# Revit family: Urinal-Monoblock-BackWaterInlet-Vitra_PluralSeries_7809B003-5330
name_source: partatom
category: Plumbing Fixtures
revit_build: Autodesk Revit 2017 (Build: 20160225_1515(x64)
units: mm (PartAtom-declared; Revit-internal decimal feet)

## family parameters
Cut with Voids When Loaded = No
Host = Face
OmniClass Number = 23.45.05.21.11.21
OmniClass Title = Urinals
Part Type = Normal
Room Calculation Point = No
Round Connector Dimension = Use Diameter
Shared = Yes

## types (10) — shared parameters
BIMobject category = Urinals
CW Connection = Yes
Default Elevation = 650 mm  [stored 2.13255 ft]
Description = VitrA Plural Monoblock urinal with integrated flushing mechanism Back inlet,
Design country = Turkey
HW Connection = No
IFC Classification = Sanitary Terminal
Main Material = Ceramic
Manufacturer = Vitra
Manufacturer name = Vitra
Masterformat 2014 Code = 22 41 13.16
Masterformat 2014 Description = Residential Urinals
MountingType = Face Mounted
NBS Referans Code = 31-93
NBS Referans Description = Urinal And Wc Fittings
Nominal Depth = 390 mm  [stored 1.27953 ft]
NominalHeight = 904 mm  [stored 2.96588 ft]
NominalWidth = 330 mm
OmniClass Code = 23-31 21 00
OmniClass Description = Urinals
Product certification = https://vitraglobal.com
Product family = Face Mounted Urinal
Product group = Plural
UNSPSC Code = 30181506
URL = https://www.vitra.com.tr
Uniclass 1.4 Code = L721
Uniclass 1.4 Description = Sanitary equipment
Uniclass 2.0 Code = PR-31-93
Uniclass 2.0 Description = Urinal And Wc Fittings
Uniclass 2015 Code = Pr_40_20_93
Uniclass 2015 Name = Urinal and WC fittings
Uniformat II Code = D2010
Uniformat II Description = Plumbing Fixtures
Vent Connection = No
Warranty Period (Year) = 10 Years
Waste Connection = Yes
Weight Net (kg) = 31,9
Youtube = https://www.youtube.com
zero-valued in all types: Cost

## per-type parameters (varying)
| type | Article No. (default) | Battery operated | Color | Mains operated | Model | Product SKU | Product data url | Product url | Secondary Material | Technical description |
| Urinal_Vitra_Plural_(White)_7809B003-5330 | 7809B003-5330 | Yes | White | No | 7809B003-5330 | 7809B003-5330 |  | https://www.vitra.com.tr | Vitra-Ceramic-White | https://www.vitra.com.tr |
| Urinal_Vitra_Plural_(MatteWhite)_ 7809B001-5330 | 7809B001-5330 | Yes | Matte White | No | 7809B001-5330 | 7809B001-5330 | https://www.vitra.com.tr |  | Vitra-MatteWhite |  |
| Urinal_Vitra_Plural_(MatteBeige)_7809B020-5330 | 7809B020-5330 | Yes | Matte Beige | No | 7809B020-5330 | 7809B020-5330 | https://www.vitra.com.tr |  | Vitra-MatteBeige |  |
| Urinal_Vitra_Plural_(MatteMink)_7809B050-5330 | 7809B050-5330 | Yes | Matte Mink | No | 7809B050-5330 | 7809B050-5330 | https://www.vitra.com.tr |  | Vitra-MatteMink |  |
| Urinal_Vitra_Plural_(MatteBlack)_7809B083-5330 | 7809B083-5330 | Yes | Matte Mink | No | 7809B083-5330 | 7809B083-5330 | https://www.vitra.com.tr |  | Vitra-MatteBlack |  |
| Urinal_Vitra_Plural_(White)_7809B003-5331 | 7809B003-5331 | No | White | Yes | 7809B003-5331 | 7809B003-5331 | https://www.vitraglobal.com |  | Vitra-Ceramic-White | https://www.vitra.com.tr |
| Urinal_Vitra_Plural_(MatteWhite)_ 7809B001-5331 | 7809B001-5331 | No | Matte White | Yes | 7809B001-5331 | 7809B001-5331 | https://www.vitraglobal.com |  | Vitra-MatteWhite |  |
| Urinal_Vitra_Plural_(MatteMink)_7809B050-5331 | 7809B050-5331 | No | Matte Mink | Yes | 7809B050-5331 | 7809B050-5331 | https://www.vitraglobal.com |  | Vitra-MatteMink |  |
| Urinal_Vitra_Plural_(MatteBlack)_7809B083-5331 | 7809B083-5331 | No | Matte Mink | Yes | 7809B083-5331 | 7809B083-5331 | https://www.vitraglobal.com |  | Vitra-MatteBlack |  |
| Urinal_Vitra_Plural_(MatteBeige)_7809B020-5331 | 7809B020-5331 | No | Matte Beige | Yes | 7809B020-5331 | 7809B020-5331 | https://www.vitraglobal.com |  | Vitra-MatteBeige |  |

note: [stored X ft] marks values corroborated as IEEE doubles in the binary element streams (Revit-internal decimal feet)

## geometry (parser evidence)
native form markers: Sweep x3
no freeform markers — native parametric forms only
